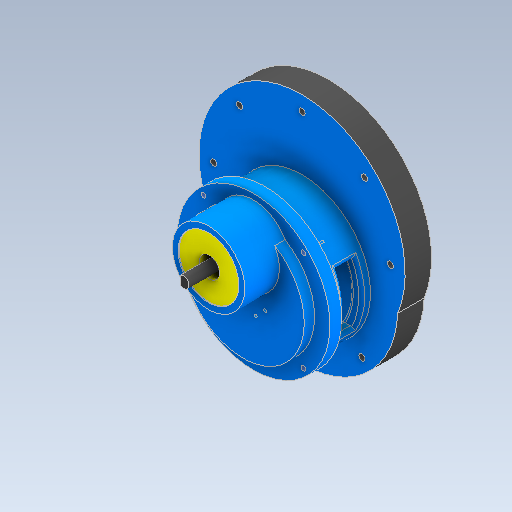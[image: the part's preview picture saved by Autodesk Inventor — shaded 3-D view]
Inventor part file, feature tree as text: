
AUTODESK INVENTOR PART (.ipt)
format: ipt  version: 2021 (Build 250183000, 183)  size: 1,105,408 bytes
history: native  units: mm
features: other x9, sketch x2
ambient origin geometry x8: Origin, YZ Plane, XZ Plane, XY Plane, X Axis, Y Axis, Z Axis, Center Point
bodies: Body1 (feature_tree)
feature tree (11):
  other  "Ensamblaje_3_MovimientoEspacio_ModuloBrida.iam"
  other  "MX-28AT_AR.ipt:1"
  other  "UnionBase_3.ipt:1"
  other  "Brida_1_MX28AT.ipt:1"
  other  "Modulo_Base_movEspacio_MX28AT_BridaEje.ipt:1"
  other  "ModuloDelantero_1_Parametrizado_MX28AT.ipt:1"
  other  "rodamiento_dummie.ipt:1"
  other  "rodamiento_dummie.ipt:2"
  other  "Sólido1"
  sketch  "Boceto14"  dims[d0=10.0mm]
  sketch  "Boceto16"
